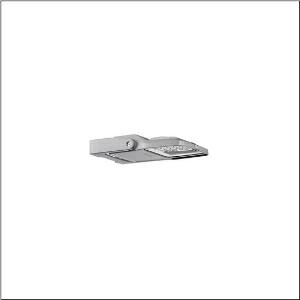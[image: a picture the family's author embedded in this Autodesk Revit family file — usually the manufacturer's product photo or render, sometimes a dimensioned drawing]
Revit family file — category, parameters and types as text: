
# Revit family: floodlight_fl_21_iq_micro___pl33t_5xa7762a4f2a_0497
name_source: partatom
category: Lighting Fixtures
units: mm (PartAtom-declared; Revit-internal decimal feet)

## family parameters
Cut with Voids When Loaded = No
Host = Face
Light Source = No
Part Type = Normal
Room Calculation Point = No
Round Connector Dimension = Use Diameter
Shared = No

## types (1)
- --- (1 x LED, 3050 lm, 23.1 W, 4000K)
    Apparent Load = 23 VA
    CIE Flux Codes = 26 75 99 100 100
    Color Rendering = 70
    Color Temperature = 4000K
    Default Elevation = 1800 mm
    Description = Floodlight FL 21 iQ micro, floodlight, primary light control with lens, of PMMA, primary optical cover: protective disc, of toughened safety glass, transparent, light distribution: PL33T, light emission: direct distribution, installation type: surface-mounted, LED, High Power LED, rated luminous flux: 3.050lm, luminous efficacy: 132lm/W, light colour: 740, colour temperature: 4000K, control: Auto-Match, Temp-Guard, Night-Set, Smart-Wire, Desk-Remote (wireless, voltage-free reading and setting of iQ features in the workshop via application-optimized NFC function/RFID function), optimised constant luminous flux control (CLO 2.0), Street-Remote, with terminal, 6-pole, mains connection: 220..240V, AC, 50/60Hz, start of lifetime: 23W, end of service life: 24W, reduction: 11W, luminaire housing, of diecast aluminium, powder-coated, Siteco® metallic grey (DB 702S), corrosivity category C5 mid according to DIN EN ISO 12944, sealing non-destructively replaceable, design bracket, of diecast aluminium, powder-coated, Siteco® metallic grey (DB 702S), protection rating (complete): IP66, insulation class (complete): insulation class II (safety insulation), certification: CE, ENEC, VDE, protection symbol: D, impact resistance: IK07, permissible operating ambient temperature: -40..+40°C, permissible operating ambient temperature for outdoor applications: -40..+50°C, standard: DIN EN 12944, LABS conformity tested according to VDMA 24364:2018-05, packaging unit: 1 piece

Light Distribution: PL33T
    Height = 65 mm
    Lamp = 1 x LED
    Lamp Light Flux = 3050 lm
    Lamp Power = 23.1 W
    Lamp count = 1
    Length = 312 mm
    Luminous efficacy = 132 lm/W
    Manufacturer = Siteco
    ModVariant = No
    Model = 5XA7762A4F2A
    Mounting Place = Wall
    Mounting Type = Surface mounted
    Number of Poles = 1
    OnlyDefault = Yes
    Power Factor = 1
    Product Name = Floodlight FL 21 iQ micro | PL33T
    Product group = floodlight | wall mounted
    ProductGroupID = 2001
    Protection Class = Protection class II
    Protection Degree = IP 66
    RLX_Detail_Level = 1
    RLX_Emergency_Light_Flux = 0 lm
    RLX_Emergency_Type = 0
    RLX_Emergency_Type_DB = No
    RlxData = <blob elided: 97305 chars, md5=52f8fcbd>
    Socket = socket
    Standby Power = 0 W
    System Light Flux = 3050 lm
    System Power = 23 W
    Type Comments = factory setting: luminous flux: 100 % | dim-lin: 254 | 455 mA
    Type Image = l_1006878.jpg
    URL = http://relux.com
    VarID = @adj_118235
    Voltage = 0 V
    Weight = 0.00 kg
    Width = 230 mm

## geometry (parser evidence)
native form markers: Blend x4, Sweep x12
no freeform markers — native parametric forms only
